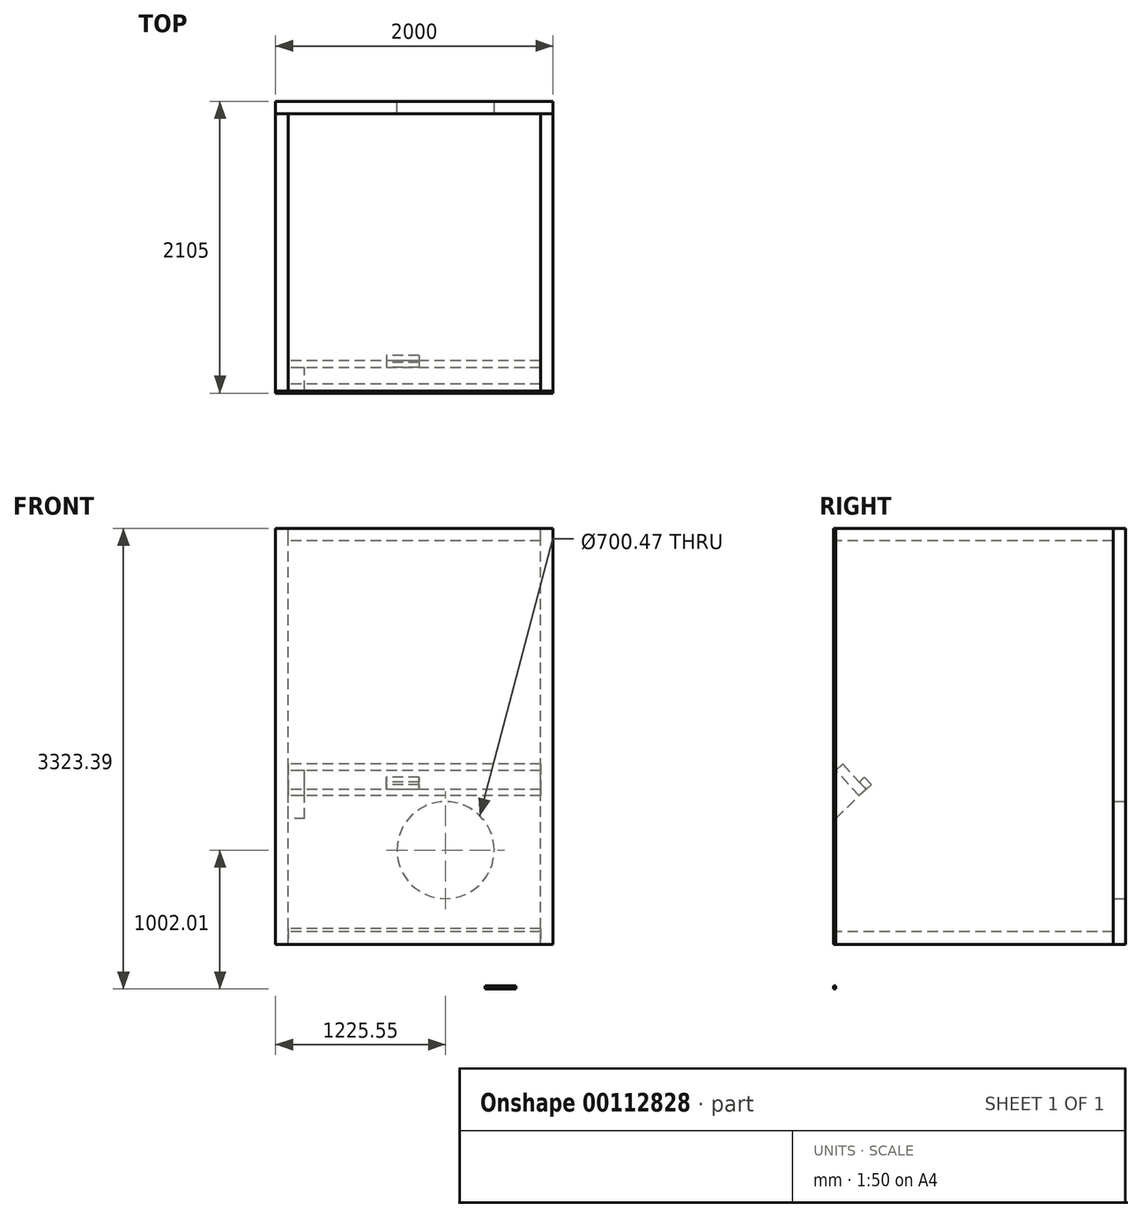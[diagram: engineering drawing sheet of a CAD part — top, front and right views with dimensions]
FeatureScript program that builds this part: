
annotation { "Feature Type Name" : "Feature", "Feature Type Description" : "" }
export const myFeature = defineFeature(function(context is Context, id is Id, definition is map)
    precondition{}
    {
        {
            var Q0;
            Q0=qCreatedBy(makeId("Front.planeOp"),FACE);
            var sketch = newSketch(context, id + "F0", { "sketchPlane" : qUnion([Q0])});
            skLineSegment(sketch, "E0.bottom", {"start": v(0, 0) * mm, "end": v(2000, 0) * mm});
            skLineSegment(sketch, "E0.top", {"start": v(0, 3000) * mm, "end": v(2000, 3000) * mm});
            skLineSegment(sketch, "E0.left", {"start": v(0, 0) * mm, "end": v(0, 3000) * mm});
            skLineSegment(sketch, "E0.right", {"start": v(2000, 0) * mm, "end": v(2000, 3000) * mm});
            skLineSegment(sketch, "E1.bottom", {"start": v(1511, -323.39) * mm, "end": v(1734.02, -323.39) * mm});
            skLineSegment(sketch, "E1.top", {"start": v(1511, -301.08) * mm, "end": v(1734.02, -301.08) * mm});
            skLineSegment(sketch, "E1.left", {"start": v(1511, -323.39) * mm, "end": v(1511, -301.08) * mm});
            skLineSegment(sketch, "E1.right", {"start": v(1734.02, -323.39) * mm, "end": v(1734.02, -301.08) * mm});
            skSolve(sketch);
        }
        {
            var Q0;
            Q0 = qSketchRegion(id + "F0", true);
            extrude(context, id + "F1", {"entities" : qUnion([Q0]), "depth" : 15 * mm});
        }
        {
            var Q0;
            Q0=makeQuery(id+"F1.opExtrude","CAP_FACE",FACE,{"disambiguationData":[OSD([sQuery(id+"F0.wireOp",EDGE,"E0.bottom"),sQuery(id+"F0.wireOp",EDGE,"E0.top"),sQuery(id+"F0.wireOp",EDGE,"E0.left"),sQuery(id+"F0.wireOp",EDGE,"E0.right")])],"isStart":true});
            var sketch = newSketch(context, id + "F2", { "sketchPlane" : qUnion([Q0])});
            skLineSegment(sketch, "E2.bottom", {"start": v(0, 0) * mm, "end": v(-90, 0) * mm});
            skLineSegment(sketch, "E2.top", {"start": v(0, 3000) * mm, "end": v(-90, 3000) * mm});
            skLineSegment(sketch, "E2.left", {"start": v(0, 0) * mm, "end": v(0, 3000) * mm});
            skLineSegment(sketch, "E2.right", {"start": v(-90, 0) * mm, "end": v(-90, 3000) * mm});
            skLineSegment(sketch, "E3.bottom", {"start": v(-90, 3000) * mm, "end": v(-90, 3000) * mm});
            skLineSegment(sketch, "E3.top", {"start": v(-90, 3000) * mm, "end": v(-90, 3000) * mm});
            skLineSegment(sketch, "E3.left", {"start": v(-90, 3000) * mm, "end": v(-90, 3000) * mm});
            skLineSegment(sketch, "E3.right", {"start": v(-90, 3000) * mm, "end": v(-90, 3000) * mm});
            skSolve(sketch);
        }
        {
            var Q0;
            Q0 = qSketchRegion(id + "F2", true);
            extrude(context, id + "F3", {"entities" : qUnion([Q0]), "depth" : 2000 * mm});
        }
        {
            var Q0;
            Q0=makeQuery(id+"F3.opExtrude","SWEPT_FACE",FACE,{"disambiguationData":[OSD([sQuery(id+"F2.wireOp",EDGE,"E2.right")])]});
            var sketch = newSketch(context, id + "F4", { "sketchPlane" : qUnion([Q0])});
            skLineSegment(sketch, "E4", {"start": v(0, 1253.2) * mm, "end": v(0, 906.67) * mm});
            skLineSegment(sketch, "E5", {"start": v(0, 906.67) * mm, "end": v(169.06, 1070.81) * mm});
            skLineSegment(sketch, "E6", {"start": v(169.06, 1070.81) * mm, "end": v(0, 1253.2) * mm});
            skSolve(sketch);
        }
        {
            var Q0;
            Q0 = qSketchRegion(id + "F4", true);
            extrude(context, id + "F5", {"entities" : qUnion([Q0]), "depth" : 120 * mm});
        }
        {
            var Q0;
            Q0=makeQuery(id+"F3.opExtrude","SWEPT_FACE",FACE,{"disambiguationData":[OSD([sQuery(id+"F2.wireOp",EDGE,"E2.right")])]});
            var sketch = newSketch(context, id + "F6", { "sketchPlane" : qUnion([Q0])});
            skLineSegment(sketch, "E7", {"start": v(169.02, 1070.83) * mm, "end": v(0, 1253.2) * mm});
            skLineSegment(sketch, "E8", {"start": v(0, 1253.2) * mm, "end": v(49.98, 1299.52) * mm});
            skLineSegment(sketch, "E9", {"start": v(49.98, 1299.52) * mm, "end": v(219, 1117.15) * mm});
            skLineSegment(sketch, "E10", {"start": v(219, 1117.15) * mm, "end": v(169.02, 1070.83) * mm});
            skSolve(sketch);
        }
        {
            var Q0;
            Q0 = qSketchRegion(id + "F6", true);
            extrude(context, id + "F7", {"entities" : qUnion([Q0]), "depth" : 1820 * mm});
        }
        {
            var Q0;
            Q0=makeQuery(id+"F7.opExtrude","SWEPT_FACE",FACE,{"disambiguationData":[OSD([sQuery(id+"F6.wireOp",EDGE,"E9")])]});
            var sketch = newSketch(context, id + "F8", { "sketchPlane" : qUnion([Q0])});
            skLineSegment(sketch, "E11.bottom", {"start": v(-1034.13, 670.48) * mm, "end": v(-799.74, 670.48) * mm});
            skLineSegment(sketch, "E11.top", {"start": v(-1034.13, 742.23) * mm, "end": v(-799.74, 742.23) * mm});
            skLineSegment(sketch, "E11.left", {"start": v(-1034.13, 670.48) * mm, "end": v(-1034.13, 742.23) * mm});
            skLineSegment(sketch, "E11.right", {"start": v(-799.74, 670.48) * mm, "end": v(-799.74, 742.23) * mm});
            skSolve(sketch);
        }
        {
            var Q0;
            Q0 = qSketchRegion(id + "F8", true);
            extrude(context, id + "F9", {"entities" : qUnion([Q0]), "depth" : 50 * mm});
        }
        {
            var Q0;
            Q0=makeQuery(id+"F3.opExtrude","SWEPT_FACE",FACE,{"disambiguationData":[OSD([sQuery(id+"F2.wireOp",EDGE,"E2.right")])]});
            var sketch = newSketch(context, id + "F10", { "sketchPlane" : qUnion([Q0])});
            skLineSegment(sketch, "E12.bottom", {"start": v(2000, 3000) * mm, "end": v(0, 3000) * mm});
            skLineSegment(sketch, "E12.top", {"start": v(2000, 2910) * mm, "end": v(0, 2910) * mm});
            skLineSegment(sketch, "E12.left", {"start": v(2000, 2910) * mm, "end": v(2000, 3000) * mm});
            skLineSegment(sketch, "E12.right", {"start": v(0, 2910) * mm, "end": v(0, 3000) * mm});
            skLineSegment(sketch, "E13.bottom", {"start": v(434.6, 2910) * mm, "end": v(667.13, 2910) * mm});
            skLineSegment(sketch, "E13.top", {"start": v(434.6, 2910) * mm, "end": v(667.13, 2910) * mm});
            skLineSegment(sketch, "E13.left", {"start": v(434.6, 2910) * mm, "end": v(434.6, 2910) * mm});
            skLineSegment(sketch, "E13.right", {"start": v(667.13, 2910) * mm, "end": v(667.13, 2910) * mm});
            skSolve(sketch);
        }
        {
            var Q0;
            Q0 = qSketchRegion(id + "F10", true);
            extrude(context, id + "F11", {"entities" : qUnion([Q0]), "depth" : 1820 * mm});
        }
        {
            var Q0;
            Q0=makeQuery(id+"F3.opExtrude","SWEPT_FACE",FACE,{"disambiguationData":[OSD([sQuery(id+"F2.wireOp",EDGE,"E2.right")])]});
            var sketch = newSketch(context, id + "F12", { "sketchPlane" : qUnion([Q0])});
            skLineSegment(sketch, "E14.bottom", {"start": v(2000, 0) * mm, "end": v(-0.06, 0) * mm});
            skLineSegment(sketch, "E14.top", {"start": v(2000, 90) * mm, "end": v(-0.06, 90) * mm});
            skLineSegment(sketch, "E14.left", {"start": v(2000, 0) * mm, "end": v(2000, 90) * mm});
            skLineSegment(sketch, "E14.right", {"start": v(-0.06, 0) * mm, "end": v(-0.06, 90) * mm});
            skLineSegment(sketch, "E15.bottom", {"start": v(0, 111.41) * mm, "end": v(-0.06, 111.41) * mm});
            skLineSegment(sketch, "E15.top", {"start": v(0, 0) * mm, "end": v(-0.06, 0) * mm});
            skLineSegment(sketch, "E15.left", {"start": v(-0.06, 111.41) * mm, "end": v(-0.06, 0) * mm});
            skLineSegment(sketch, "E15.right", {"start": v(0, 111.41) * mm, "end": v(0, 0) * mm});
            skSolve(sketch);
        }
        {
            var Q0;
            Q0 = qSketchRegion(id + "F12", true);
            extrude(context, id + "F13", {"entities" : qUnion([Q0]), "depth" : 1820 * mm});
        }
        {
            var Q0;
            Q0=makeQuery(id+"F11.opExtrude","CAP_FACE",FACE,{"disambiguationData":[OSD([sQuery(id+"F10.wireOp",EDGE,"E12.bottom"),sQuery(id+"F10.wireOp",EDGE,"E12.top"),sQuery(id+"F10.wireOp",EDGE,"E12.left"),sQuery(id+"F10.wireOp",EDGE,"E12.right"),sQuery(id+"F10.wireOp",EDGE,"E13.top")])],"isStart":false});
            var sketch = newSketch(context, id + "F14", { "sketchPlane" : qUnion([Q0])});
            skLineSegment(sketch, "E16.bottom", {"start": v(2000, 3000) * mm, "end": v(0, 3000) * mm});
            skLineSegment(sketch, "E16.top", {"start": v(2000, 0) * mm, "end": v(0, 0) * mm});
            skLineSegment(sketch, "E16.left", {"start": v(2000, 3000) * mm, "end": v(2000, 0) * mm});
            skLineSegment(sketch, "E16.right", {"start": v(0, 3000) * mm, "end": v(0, 0) * mm});
            skSolve(sketch);
        }
        {
            var Q0;
            Q0 = qSketchRegion(id + "F14", true);
            extrude(context, id + "F15", {"entities" : qUnion([Q0]), "depth" : 90 * mm});
        }
        {
            var Q0;
            Q0=makeQuery(id+"F15.opExtrude","SWEPT_FACE",FACE,{"disambiguationData":[OSD([sQuery(id+"F14.wireOp",EDGE,"E16.left")])]});
            var sketch = newSketch(context, id + "F16", { "sketchPlane" : qUnion([Q0])});
            skLineSegment(sketch, "E17.bottom", {"start": v(-2000, 3000) * mm, "end": v(0, 3000) * mm});
            skLineSegment(sketch, "E17.top", {"start": v(-2000, 0) * mm, "end": v(0, 0) * mm});
            skLineSegment(sketch, "E17.left", {"start": v(-2000, 3000) * mm, "end": v(-2000, 0) * mm});
            skLineSegment(sketch, "E17.right", {"start": v(0, 3000) * mm, "end": v(0, 0) * mm});
            skSolve(sketch);
        }
        {
            var Q0;
            Q0 = qSketchRegion(id + "F16", true);
            extrude(context, id + "F17", {"entities" : qUnion([Q0]), "depth" : 90 * mm});
        }
        {
            var Q0;
            Q0=makeQuery(id+"F17.opExtrude","CAP_FACE",FACE,{"disambiguationData":[OSD([sQuery(id+"F16.wireOp",EDGE,"E17.bottom"),sQuery(id+"F16.wireOp",EDGE,"E17.top"),sQuery(id+"F16.wireOp",EDGE,"E17.left"),sQuery(id+"F16.wireOp",EDGE,"E17.right")])],"isStart":false});
            var sketch = newSketch(context, id + "F18", { "sketchPlane" : qUnion([Q0])});
            skCircle(sketch, "E18", {"center": v(-1225.55, 678.62) * mm, "radius": 350.24 * mm});
            skSolve(sketch);
        }
        {
            var Q0;
            Q0 = qSketchRegion(id + "F18", true);
            extrude(context, id + "F19", {"entities" : qUnion([Q0]), "operationType" : NewBodyOperationType.REMOVE, "oppositeDirection" : true, "depth" : 90 * mm});
        }
    });
